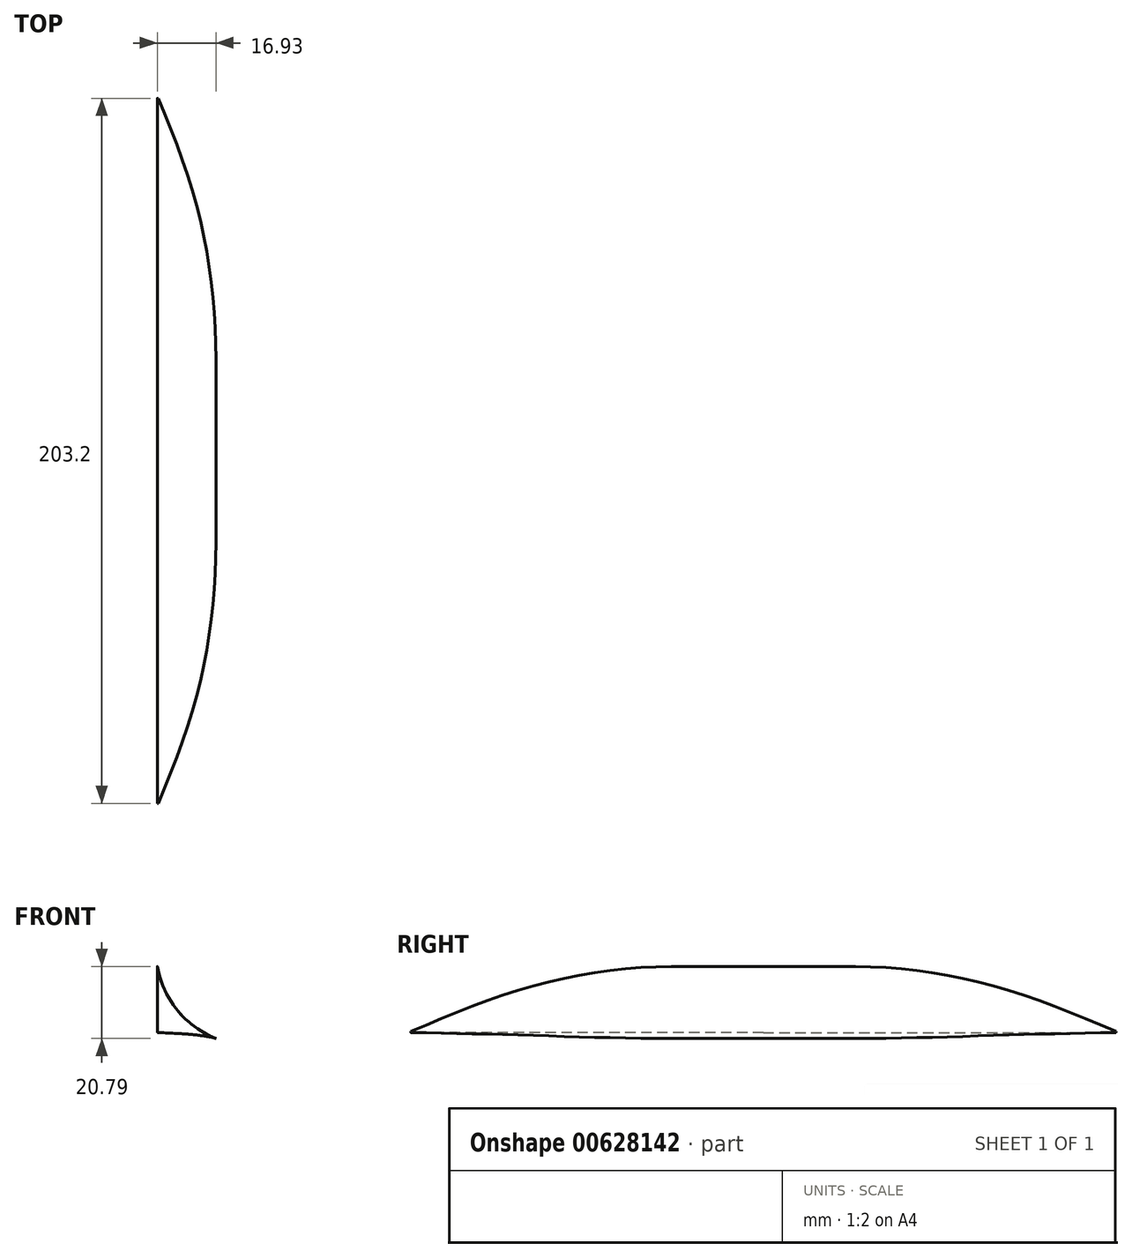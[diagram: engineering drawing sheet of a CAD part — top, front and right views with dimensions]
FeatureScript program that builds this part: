
annotation { "Feature Type Name" : "Feature", "Feature Type Description" : "" }
export const myFeature = defineFeature(function(context is Context, id is Id, definition is map)
    precondition{}
    {
        {
            assignVariable(context, id + "F0", {"name" : "taperLength", "anyValue" : 76.2 * mm});
        }
        {
            assignVariable(context, id + "F1", {"name" : "totalLength", "anyValue" : 203.2 * mm});
        }
        {
            assignVariable(context, id + "F2", {"name" : "pinchRatio", "anyValue" : 0.7});
        }
        {
            var Q0;
            Q0=qCreatedBy(makeId("Front.planeOp"),FACE);
            var sketch = newSketch(context, id + "F3", { "sketchPlane" : qUnion([Q0])});
            skCircle(sketch, "E0", {"center": v(0, 0) * mm, "radius": 83.82 * mm, "construction": true});
            skLineSegment(sketch, "E1", {"start": v(0, 83.82) * mm, "end": v(0, 102.87) * mm});
            skArc(sketch, "E2", {"start": v(0, 102.87) * mm, "mid": v(5.76, 90.28) * mm, "end": v(16.93, 82.1) * mm});
            skLineSegment(sketch, "E3", {"start": v(0, 102.87) * mm, "end": v(2.18, 90.5) * mm, "construction": true});
            skLineSegment(sketch, "E4", {"start": v(16.93, 82.1) * mm, "end": v(9.45, 83.63) * mm, "construction": true});
            skLineSegment(sketch, "E5", {"start": v(16.93, 82.1) * mm, "end": v(10.03, 84.83) * mm, "construction": true});
            skArc(sketch, "E6", {"start": v(0, 83.82) * mm, "mid": v(8.5, 83.39) * mm, "end": v(16.93, 82.1) * mm});
            skSolve(sketch);
        }
        {
            var Q0;
            Q0=qCreatedBy(makeId("Front.planeOp"),FACE);
            cPlane(context, id + "F4", {"entities" : qUnion([Q0]), "cplaneType" : CPlaneType.OFFSET, "offset" : getVariable(context, 'totalLength') / 2 - getVariable(context, 'taperLength'), "width" : 152.4 * mm, "height" : 152.4 * mm});
        }
        {
            var Q0;
            Q0=qCreatedBy(id+"F4.planeOp",FACE);
            var sketch = newSketch(context, id + "F5", { "sketchPlane" : qUnion([Q0])});
            skCircle(sketch, "E7", {"center": v(0, 0) * mm, "radius": 83.82 * mm, "construction": true});
            skLineSegment(sketch, "E8", {"start": v(0, 83.82) * mm, "end": v(0, 102.87) * mm});
            skArc(sketch, "E9", {"start": v(0, 102.87) * mm, "mid": v(5.76, 90.28) * mm, "end": v(16.93, 82.1) * mm});
            skLineSegment(sketch, "E10", {"start": v(0, 102.87) * mm, "end": v(2.18, 90.5) * mm, "construction": true});
            skLineSegment(sketch, "E11", {"start": v(16.93, 82.1) * mm, "end": v(3.75, 84.81) * mm, "construction": true});
            skLineSegment(sketch, "E12", {"start": v(16.93, 82.1) * mm, "end": v(4.43, 87.06) * mm, "construction": true});
            skArc(sketch, "E13", {"start": v(0, 83.82) * mm, "mid": v(8.5, 83.39) * mm, "end": v(16.93, 82.1) * mm});
            skSolve(sketch);
        }
        {
            var Q0;
            Q0=qCreatedBy(makeId("Front.planeOp"),FACE);
            cPlane(context, id + "F6", {"entities" : qUnion([Q0]), "cplaneType" : CPlaneType.OFFSET, "offset" : 0.99 * (getVariable(context, 'totalLength') / 2 - getVariable(context, 'taperLength')), "width" : 152.4 * mm, "height" : 152.4 * mm});
        }
        {
            var Q0;
            Q0=qCreatedBy(id+"F6.planeOp",FACE);
            var sketch = newSketch(context, id + "F7", { "sketchPlane" : qUnion([Q0])});
            skCircle(sketch, "E14", {"center": v(0, 0) * mm, "radius": 83.82 * mm, "construction": true});
            skLineSegment(sketch, "E15", {"start": v(0, 83.82) * mm, "end": v(0, 102.87) * mm});
            skArc(sketch, "E16", {"start": v(0, 102.87) * mm, "mid": v(5.76, 90.28) * mm, "end": v(16.93, 82.1) * mm});
            skLineSegment(sketch, "E17", {"start": v(0, 102.87) * mm, "end": v(2.18, 90.5) * mm, "construction": true});
            skLineSegment(sketch, "E18", {"start": v(16.93, 82.1) * mm, "end": v(11.77, 83.16) * mm, "construction": true});
            skLineSegment(sketch, "E19", {"start": v(16.93, 82.1) * mm, "end": v(12.22, 83.96) * mm, "construction": true});
            skArc(sketch, "E20", {"start": v(0, 83.82) * mm, "mid": v(8.5, 83.39) * mm, "end": v(16.93, 82.1) * mm});
            skSolve(sketch);
        }
        {
            var Q0;
            Q0=qCreatedBy(id+"F4.planeOp",FACE);
            cPlane(context, id + "F8", {"entities" : qUnion([Q0]), "cplaneType" : CPlaneType.OFFSET, "offset" : getVariable(context, 'taperLength') * getVariable(context, 'pinchRatio'), "width" : 152.4 * mm, "height" : 152.4 * mm});
        }
        {
            var Q0;
            Q0=qCreatedBy(id+"F8.planeOp",FACE);
            var sketch = newSketch(context, id + "F9", { "sketchPlane" : qUnion([Q0])});
            skCircle(sketch, "E21", {"center": v(0, 0) * mm, "radius": 83.82 * mm, "construction": true});
            skLineSegment(sketch, "E22", {"start": v(0, 83.82) * mm, "end": v(0, 93.35) * mm});
            skArc(sketch, "E23", {"start": v(0, 93.35) * mm, "mid": v(3.06, 87.06) * mm, "end": v(8.99, 83.34) * mm});
            skLineSegment(sketch, "E24", {"start": v(0, 93.35) * mm, "end": v(0.55, 90.2) * mm, "construction": true});
            skLineSegment(sketch, "E25", {"start": v(8.99, 83.34) * mm, "end": v(1.62, 84.13) * mm, "construction": true});
            skLineSegment(sketch, "E26", {"start": v(8.99, 83.34) * mm, "end": v(2.09, 85.34) * mm, "construction": true});
            skArc(sketch, "E27", {"start": v(0, 83.82) * mm, "mid": v(4.5, 83.7) * mm, "end": v(8.99, 83.34) * mm});
            skSolve(sketch);
        }
        {
            var Q0;
            Q0=qCreatedBy(id+"F8.planeOp",FACE);
            cPlane(context, id + "F10", {"entities" : qUnion([Q0]), "cplaneType" : CPlaneType.OFFSET, "offset" : getVariable(context, 'taperLength') * (1 - getVariable(context, 'pinchRatio')), "width" : 152.4 * mm, "height" : 152.4 * mm});
        }
        {
            var Q0;
            Q0=qCreatedBy(id+"F10.planeOp",FACE);
            var sketch = newSketch(context, id + "F11", { "sketchPlane" : qUnion([Q0])});
            skCircle(sketch, "E28", {"center": v(0, 0) * mm, "radius": 83.82 * mm, "construction": true});
            skLineSegment(sketch, "E29", {"start": v(0, 83.82) * mm, "end": v(0, 84.12) * mm});
            skArc(sketch, "E30", {"start": v(0, 84.12) * mm, "mid": v(0.1, 83.92) * mm, "end": v(0.3, 83.82) * mm});
            skLineSegment(sketch, "E31", {"start": v(0, 84.12) * mm, "end": v(0.24, 82.75) * mm, "construction": true});
            skLineSegment(sketch, "E32", {"start": v(7.15, 83.8) * mm, "end": v(0.3, 83.82) * mm, "construction": true});
            skLineSegment(sketch, "E33", {"start": v(4.01, 83.15) * mm, "end": v(0.3, 83.82) * mm, "construction": true});
            skArc(sketch, "E34", {"start": v(0, 83.82) * mm, "mid": v(0.15, 83.82) * mm, "end": v(0.3, 83.82) * mm});
            skSolve(sketch);
        }
        {
            var Q0;
            Q0=makeQuery(id+"F3.imprint","IMPRINT",FACE,{"disambiguationData":[TD([[makeQuery(id+"F3.imprint","IMPRINT",EDGE,{"derivedFrom":sQuery(id+"F3.wireOp",EDGE,"E1")}),-1.0]])]});
            var Q1;
            Q1 = qSketchRegion(id + "F7", true);
            var Q2;
            Q2 = qSketchRegion(id + "F5", true);
            var Q3;
            Q3 = qSketchRegion(id + "F9", true);
            var Q4;
            Q4 = qSketchRegion(id + "F11", true);
            loft(context, id + "F12", {"sheetProfilesArray" : [{ "sheetProfileEntities" : qUnion([Q0]) }, { "sheetProfileEntities" : qUnion([Q1]) }, { "sheetProfileEntities" : qUnion([Q2]) }, { "sheetProfileEntities" : qUnion([Q3]) }, { "sheetProfileEntities" : qUnion([Q4]) }]});
        }
        {
            var Q0;
            Q0=makeQuery(id+"F12.opLoft","SWEPT_BODY",BODY,{"disambiguationData":[OSD([sQuery(id+"F3.wireOp",EDGE,"E1"),sQuery(id+"F9.wireOp",EDGE,"E22"),makeQuery(id+"F5.imprint","IMPRINT",FACE,{"disambiguationData":[TD([[makeQuery(id+"F5.imprint","IMPRINT",EDGE,{"derivedFrom":sQuery(id+"F5.wireOp",EDGE,"E8")}),-1.0]])]}),makeQuery(id+"F11.imprint","IMPRINT",FACE,{"disambiguationData":[TD([[makeQuery(id+"F11.imprint","IMPRINT",EDGE,{"derivedFrom":sQuery(id+"F11.wireOp",EDGE,"E29")}),-1.0]])]})])]});
            var Q1;
            Q1=qCreatedBy(makeId("Front.planeOp"),FACE);
            mirror(context, id + "F13", {"operationType" : NewBodyOperationType.ADD, "entities" : qUnion([Q0]), "mirrorPlane" : qUnion([Q1])});
        }
    });
